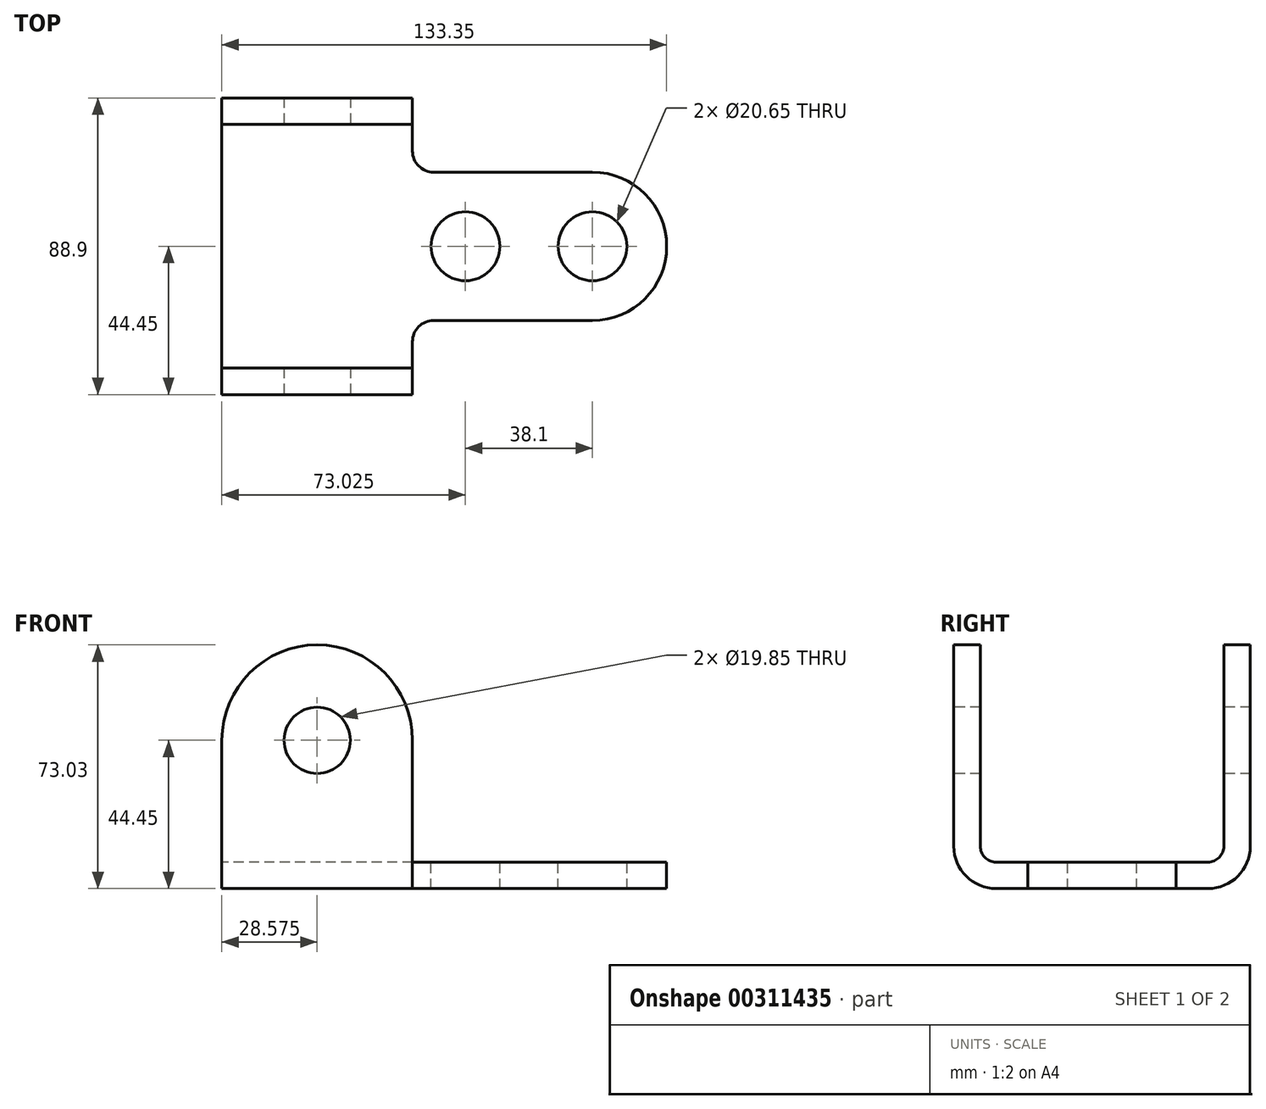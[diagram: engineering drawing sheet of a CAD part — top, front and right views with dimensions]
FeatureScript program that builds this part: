
annotation { "Feature Type Name" : "Feature", "Feature Type Description" : "" }
export const myFeature = defineFeature(function(context is Context, id is Id, definition is map)
    precondition{}
    {
        {
            var Q0;
            Q0=qCreatedBy(makeId("Right.planeOp"),FACE);
            var sketch = newSketch(context, id + "F0", { "sketchPlane" : qUnion([Q0])});
            skLineSegment(sketch, "E0", {"start": v(0, 0) * mm, "end": v(-31.75, 0) * mm});
            skLineSegment(sketch, "E1", {"start": v(-44.45, 12.7) * mm, "end": v(-44.45, 73.03) * mm});
            skLineSegment(sketch, "E2", {"start": v(-44.45, 73.03) * mm, "end": v(-36.51, 73.03) * mm});
            skLineSegment(sketch, "E3", {"start": v(-36.51, 73.03) * mm, "end": v(-36.51, 12.7) * mm});
            skLineSegment(sketch, "E4", {"start": v(-31.75, 7.94) * mm, "end": v(31.75, 7.94) * mm});
            skLineSegment(sketch, "E5", {"start": v(36.51, 12.7) * mm, "end": v(36.51, 73.03) * mm});
            skLineSegment(sketch, "E6", {"start": v(36.51, 73.03) * mm, "end": v(44.45, 73.03) * mm});
            skLineSegment(sketch, "E7", {"start": v(44.45, 73.03) * mm, "end": v(44.45, 12.7) * mm});
            skLineSegment(sketch, "E8", {"start": v(0, 0) * mm, "end": v(31.75, 0) * mm});
            skPoint(sketch, "E9.visualSharp", {"position": v(-44.45, 0) * mm});
            skArc(sketch, "E9.filletArc", {"start": v(-44.45, 12.7) * mm, "mid": v(-40.73, 3.72) * mm, "end": v(-31.75, 0) * mm});
            skPoint(sketch, "E10.visualSharp", {"position": v(-36.51, 7.94) * mm});
            skArc(sketch, "E10.filletArc", {"start": v(-36.51, 12.7) * mm, "mid": v(-35.12, 9.33) * mm, "end": v(-31.75, 7.94) * mm});
            skPoint(sketch, "E11.visualSharp", {"position": v(44.45, 0) * mm});
            skArc(sketch, "E11.filletArc", {"start": v(31.75, 0) * mm, "mid": v(40.73, 3.72) * mm, "end": v(44.45, 12.7) * mm});
            skPoint(sketch, "E12.visualSharp", {"position": v(36.51, 7.94) * mm});
            skArc(sketch, "E12.filletArc", {"start": v(31.75, 7.94) * mm, "mid": v(35.12, 9.33) * mm, "end": v(36.51, 12.7) * mm});
            skSolve(sketch);
        }
        {
            var Q0;
            Q0=makeQuery(id+"F0.imprint","IMPRINT",FACE,{"disambiguationData":[TD([[makeQuery(id+"F0.imprint","IMPRINT",EDGE,{"derivedFrom":sQuery(id+"F0.wireOp",EDGE,"E0")}),-1.0]])]});
            extrude(context, id + "F1", {"entities" : qUnion([Q0]), "depth" : 57.15 * mm});
        }
        {
            var Q0;
            Q0=makeQuery(id+"F1.opExtrude","SWEPT_FACE",FACE,{"disambiguationData":[OSD([sQuery(id+"F0.wireOp",EDGE,"E4")])]});
            var sketch = newSketch(context, id + "F2", { "sketchPlane" : qUnion([Q0])});
            skLineSegment(sketch, "E13.0", {"start": v(57.15, 28.58) * mm, "end": v(57.15, 31.75) * mm});
            skLineSegment(sketch, "E14", {"start": v(57.15, 0) * mm, "end": v(124.36, 0) * mm, "construction": true});
            skArc(sketch, "E15", {"start": v(111.12, -22.22) * mm, "mid": v(133.35, 0) * mm, "end": v(111.12, 22.23) * mm});
            skCircle(sketch, "E16", {"center": v(73.03, 0) * mm, "radius": 10.33 * mm});
            skCircle(sketch, "E17", {"center": v(111.12, 0) * mm, "radius": 10.33 * mm});
            skLineSegment(sketch, "E18", {"start": v(111.12, 22.23) * mm, "end": v(63.5, 22.23) * mm});
            skLineSegment(sketch, "E19", {"start": v(111.12, -22.22) * mm, "end": v(63.5, -22.22) * mm});
            skPoint(sketch, "E20.newPointB", {"position": v(57.15, -31.75) * mm});
            skArc(sketch, "E20.filletArc", {"start": v(57.15, 28.58) * mm, "mid": v(59, 24.08) * mm, "end": v(63.5, 22.23) * mm});
            skLineSegment(sketch, "E21", {"start": v(57.15, -28.57) * mm, "end": v(57.15, -31.75) * mm});
            skPoint(sketch, "E22.visualSharp", {"position": v(57.15, -22.22) * mm});
            skArc(sketch, "E22.filletArc", {"start": v(63.5, -22.22) * mm, "mid": v(59, -24.08) * mm, "end": v(57.15, -28.57) * mm});
            skLineSegment(sketch, "E23", {"start": v(57.15, 28.58) * mm, "end": v(57.15, -28.58) * mm});
            skSolve(sketch);
        }
        {
            var Q0;
            Q0=makeQuery(id+"F2.imprint","IMPRINT",FACE,{"disambiguationData":[TD([[makeQuery(id+"F2.imprint","IMPRINT",EDGE,{"derivedFrom":sQuery(id+"F2.wireOp",EDGE,"E15")}),1.0]])]});
            extrude(context, id + "F3", {"entities" : qUnion([Q0]), "operationType" : NewBodyOperationType.ADD, "oppositeDirection" : true, "depth" : 7.94 * mm});
        }
        {
            var Q0;
            Q0=makeQuery(id+"F1.opExtrude","SWEPT_FACE",FACE,{"disambiguationData":[OSD([sQuery(id+"F0.wireOp",EDGE,"E1")])]});
            var sketch = newSketch(context, id + "F4", { "sketchPlane" : qUnion([Q0])});
            skLineSegment(sketch, "E24.0.0", {"start": v(0, 73.03) * mm, "end": v(0, 12.7) * mm});
            skLineSegment(sketch, "E24.0.1", {"start": v(0, 12.7) * mm, "end": v(57.15, 12.7) * mm});
            skLineSegment(sketch, "E24.0.2", {"start": v(57.15, 12.7) * mm, "end": v(57.15, 73.03) * mm});
            skLineSegment(sketch, "E24.0.3", {"start": v(57.15, 73.03) * mm, "end": v(0, 73.03) * mm});
            skLineSegment(sketch, "E25", {"start": v(28.58, 73.03) * mm, "end": v(28.58, 44.45) * mm, "construction": true});
            skCircle(sketch, "E26", {"center": v(28.58, 44.45) * mm, "radius": 28.58 * mm});
            skCircle(sketch, "E27", {"center": v(28.58, 44.45) * mm, "radius": 9.92 * mm});
            skSolve(sketch);
        }
        {
            var Q0;
            Q0=makeQuery(id+"F4.imprint","IMPRINT",FACE,{"disambiguationData":[TD([[makeQuery(id+"F4.imprint","IMPRINT",EDGE,{"derivedFrom":sQuery(id+"F4.wireOp",EDGE,"E27")}),1.0]])]});
            var Q1;
            {var subQ0=sQuery(id+"F4.wireOp",EDGE,"E24.0.3");var subQ1=sQuery(id+"F4.wireOp",EDGE,"E24.0.0");var subQ2=makeQuery(id+"F4.imprint","INTERSECT",VERTEX,{"derivedFrom":[subQ1,subQ0]});Q1=makeQuery(id+"F4.imprint","IMPRINT",FACE,{"disambiguationData":[TD([[makeQuery(id+"F4.imprint","IMPRINT",EDGE,{"disambiguationData":[TD([[subQ2,1.0]])],"derivedFrom":subQ1}),-1.0]])]});}
            var Q2;
            {var subQ0=sQuery(id+"F4.wireOp",EDGE,"E24.0.3");var subQ1=sQuery(id+"F4.wireOp",EDGE,"E24.0.2");var subQ2=makeQuery(id+"F4.imprint","INTERSECT",VERTEX,{"derivedFrom":[subQ1,subQ0]});Q2=makeQuery(id+"F4.imprint","IMPRINT",FACE,{"disambiguationData":[TD([[makeQuery(id+"F4.imprint","IMPRINT",EDGE,{"disambiguationData":[TD([[subQ2,1.0]])],"derivedFrom":subQ1}),1.0]])]});}
            extrude(context, id + "F5", {"entities" : qUnion([Q0, Q1, Q2]), "operationType" : NewBodyOperationType.REMOVE, "oppositeDirection" : true, "depth" : 88.9 * mm});
        }
    });
